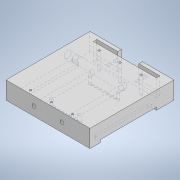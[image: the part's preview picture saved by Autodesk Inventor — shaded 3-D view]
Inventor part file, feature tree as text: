
AUTODESK INVENTOR PART (.ipt)
format: ipt  version: 2022 (Build 260153000, 153)  size: 263,680 bytes
history: native  units: in
note: dims shown in document units (in); Inventor stores cm internally (conversion verified against a paired STEP export)
features: sketch x9, hole x6, extrude x4
ambient origin geometry x8: Origin, YZ Plane, XZ Plane, XY Plane, X Axis, Y Axis, Z Axis, Center Point
bodies: Solid1 (feature_tree)
feature tree (19):
  extrude  "Extrusion1"  Depth=3.0in
  extrude  "Extrusion2"  Depth=0.75in
  sketch  "Sketch4"  dims[d5=0.25in d6=0.125in]
  hole  "Hole1"  [1 undecoded]
  hole  "Hole2"  [1 undecoded]
  extrude  "Extrusion4"  Depth=0.125in
  hole  "Hole3"  [1 undecoded]
  hole  "Hole4"  [1 undecoded]
  hole  "Hole5"  [1 undecoded]
  hole  "Hole6"  [1 undecoded]
  extrude  "Extrusion5"  Depth=0.0156in
  sketch  "Sketch1"  dims[d0=3.0in d1=3.0in]
  sketch  "Sketch3"  dims[d2=0.625in d3=0.0in d4=0.75in]
  sketch  "Sketch6"  dims[d7=0.75in d8=0.0in d9=0.0in]
  sketch  "Sketch7"  dims[d10=0.75in d11=0.125in]
  sketch  "Sketch8"  dims[d12=0.125in d13=0.125in]
  sketch  "Sketch9"  dims[d14=0.0561in d15=0.146in d16=0.375in d17=0.25in d18=0.5635in d19=0.375in d20=0.8108in d21=0.25in]
  sketch  "Sketch10"  dims[d22=0.25in]
  sketch  "Sketch11"  dims[d23=0.081in d24=0.146in d25=0.146in d26=0.25in d27=0.5635in d28=0.375in d29=0.8108in d32=0.25in d33=2.0in d34=0.375in d35=0.25in d36=2.0in d37=0.375in d38=0.0938in d39=0.0in d40=0.75in d41=0.75in d42=0.125in d43=0.0667in d44=0.425in d45=0.172in d46=0.25in d47=0.5635in d48=1.0in d49=0.8108in d50=0.425in d51=0.0625in d52=0.625in d53=0.3125in d54=0.8in d55=0.234in d56=0.2711in d57=0.0246in d58=0.2346in d59=0.375in d60=0.25in d61=0.5635in d62=2.0in d63=0.8108in d64=1.0in d65=3.0in d66=2.0in d67=0.625in d68=0.3125in d69=0.145in d70=0.38in d71=0.0246in d72=0.2346in d73=0.375in d74=0.25in d75=0.5635in d76=2.15in d77=0.8108in d78=1.0in d79=1.0in d80=0.625in d81=2.0in d82=0.096in d83=0.271in d84=0.375in d85=0.25in d86=0.5635in d87=0.25in d88=0.8108in d89=0.05in d90=0.05in d91=0.0156in d92=0.0in]
note: 6 required parameter values undecoded (feature->parameter linkage not recoverable at this tier; creation-order binding heuristic only, values carry confidence <= 0.55)
